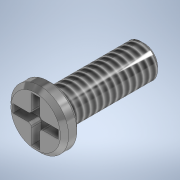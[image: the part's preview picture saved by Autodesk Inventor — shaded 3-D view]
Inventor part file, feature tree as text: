
AUTODESK INVENTOR PART (.ipt)
format: ipt  version: 2021 (Build 250183000, 183)  size: 158,720 bytes
history: native  units: mm
features: extrude x3, sketch x3, chamfer x2, other x1, thread x1, fillet x1
ambient origin geometry x8: Origin, YZ Plane, XZ Plane, XY Plane, X Axis, Y Axis, Z Axis, Center Point
bodies: Body1 (feature_tree)
feature tree (11):
  other  "Sólido1"
  extrude  "Extrusão1"  Depth=5.59mm TaperAngle=0.0deg
  extrude  "Extrusão2"  Depth=1.0mm TaperAngle=0.0deg
  extrude  "Extrusão3"  Depth=0.5mm
  thread  "Rosca1"  [1 undecoded]
  fillet  "Arredondamento2"  Radius=2.75mm
  chamfer  "Chanfro1"  Distance=0.6mm
  chamfer  "Chanfro2"  Distance=15.255mm
  sketch  "Esboço1"  dims[d0=2.0mm d1=5.59mm d2=0.0mm]
  sketch  "Esboço2"  dims[d3=3.5mm d4=1.0mm d5=0.0mm]
  sketch  "Esboço3"  dims[d6=0.5mm d7=0.5mm d8=2.75mm d9=2.75mm d10=0.6mm d11=0.0mm d13=15.255mm d14=0.0mm d15=0.2mm d16=0.25mm d17=2.0mm d18=45.0deg d19=0.2mm d20=2.0mm d21=45.0deg]
note: 1 required parameter value undecoded (feature->parameter linkage not recoverable at this tier; creation-order binding heuristic only, values carry confidence <= 0.55)
